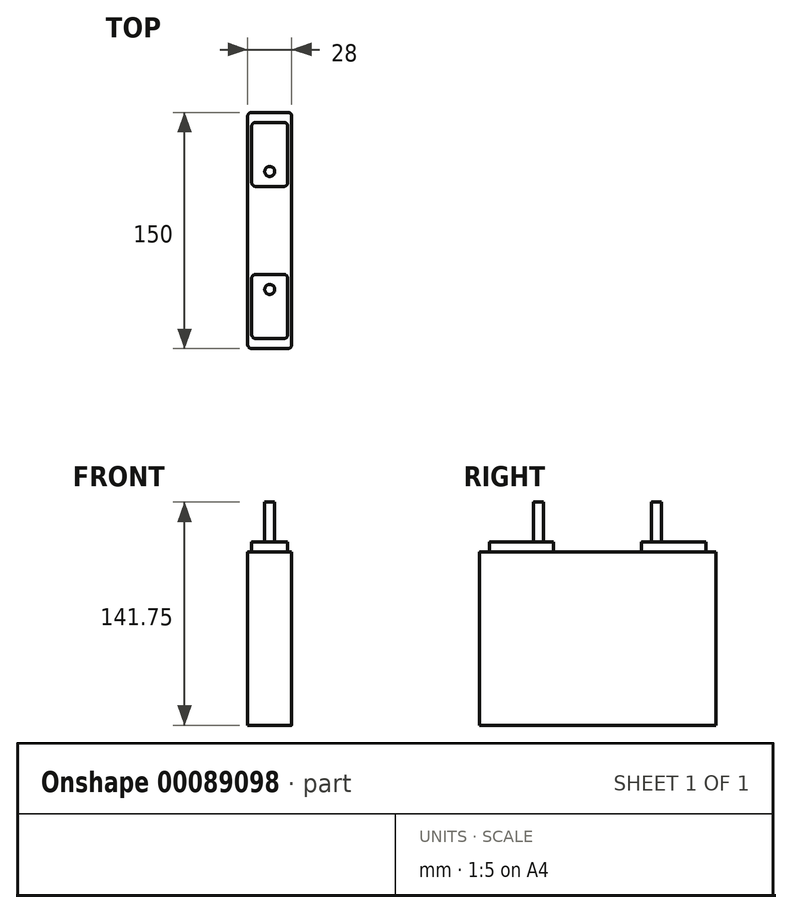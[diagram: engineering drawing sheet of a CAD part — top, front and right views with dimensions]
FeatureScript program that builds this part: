
annotation { "Feature Type Name" : "Feature", "Feature Type Description" : "" }
export const myFeature = defineFeature(function(context is Context, id is Id, definition is map)
    precondition{}
    {
        {
            var Q0;
            Q0=qCreatedBy(makeId("Top.planeOp"),FACE);
            var sketch = newSketch(context, id + "F0", { "sketchPlane" : qUnion([Q0])});
            skLineSegment(sketch, "E0.bottom", {"start": v(11.46, 75) * mm, "end": v(-11.46, 75) * mm});
            skLineSegment(sketch, "E0.top", {"start": v(11.46, -75) * mm, "end": v(-11.46, -75) * mm});
            skLineSegment(sketch, "E0.left", {"start": v(14, 72.46) * mm, "end": v(14, -72.46) * mm});
            skLineSegment(sketch, "E0.right", {"start": v(-14, 72.46) * mm, "end": v(-14, -72.46) * mm});
            skPoint(sketch, "E0.middle", {"position": v(0, 0) * mm});
            skPoint(sketch, "E1.visualSharp", {"position": v(14, -75) * mm});
            skArc(sketch, "E1.filletArc", {"start": v(11.46, -75) * mm, "mid": v(13.26, -74.26) * mm, "end": v(14, -72.46) * mm});
            skPoint(sketch, "E2.visualSharp", {"position": v(-14, -75) * mm});
            skArc(sketch, "E2.filletArc", {"start": v(-14, -72.46) * mm, "mid": v(-13.26, -74.26) * mm, "end": v(-11.46, -75) * mm});
            skPoint(sketch, "E3.visualSharp", {"position": v(-14, 75) * mm});
            skArc(sketch, "E3.filletArc", {"start": v(-11.46, 75) * mm, "mid": v(-13.26, 74.26) * mm, "end": v(-14, 72.46) * mm});
            skPoint(sketch, "E4.visualSharp", {"position": v(14, 75) * mm});
            skArc(sketch, "E4.filletArc", {"start": v(14, 72.46) * mm, "mid": v(13.26, 74.26) * mm, "end": v(11.46, 75) * mm});
            skSolve(sketch);
        }
        {
            var Q0;
            Q0 = qSketchRegion(id + "F0", true);
            extrude(context, id + "F1", {"entities" : qUnion([Q0]), "depth" : 110 * mm});
        }
        {
            var Q0;
            Q0=makeQuery(id+"F1.opExtrude","CAP_FACE",FACE,{"disambiguationData":[OSD([sQuery(id+"F0.wireOp",EDGE,"E0.bottom"),sQuery(id+"F0.wireOp",EDGE,"E0.top"),sQuery(id+"F0.wireOp",EDGE,"E0.left"),sQuery(id+"F0.wireOp",EDGE,"E0.right"),sQuery(id+"F0.wireOp",EDGE,"E1.filletArc"),sQuery(id+"F0.wireOp",EDGE,"E2.filletArc"),sQuery(id+"F0.wireOp",EDGE,"E3.filletArc"),sQuery(id+"F0.wireOp",EDGE,"E4.filletArc")])],"isStart":false});
            var sketch = newSketch(context, id + "F2", { "sketchPlane" : qUnion([Q0])});
            skLineSegment(sketch, "E5.bottom", {"start": v(-8.92, -68.65) * mm, "end": v(8.92, -68.65) * mm});
            skLineSegment(sketch, "E5.top", {"start": v(-8.92, -27.94) * mm, "end": v(8.92, -27.94) * mm});
            skLineSegment(sketch, "E5.left", {"start": v(-11.46, -66.11) * mm, "end": v(-11.46, -30.48) * mm});
            skLineSegment(sketch, "E5.right", {"start": v(11.46, -66.11) * mm, "end": v(11.46, -30.48) * mm});
            skLineSegment(sketch, "E6.bottom", {"start": v(-8.92, 68.65) * mm, "end": v(8.92, 68.65) * mm});
            skLineSegment(sketch, "E6.top", {"start": v(-8.92, 27.94) * mm, "end": v(8.92, 27.94) * mm});
            skLineSegment(sketch, "E6.left", {"start": v(-11.46, 66.11) * mm, "end": v(-11.46, 30.48) * mm});
            skLineSegment(sketch, "E6.right", {"start": v(11.46, 66.11) * mm, "end": v(11.46, 30.48) * mm});
            skPoint(sketch, "E7.visualSharp", {"position": v(11.46, -68.65) * mm});
            skArc(sketch, "E7.filletArc", {"start": v(8.92, -68.65) * mm, "mid": v(10.72, -67.9) * mm, "end": v(11.46, -66.11) * mm});
            skPoint(sketch, "E8.visualSharp", {"position": v(-11.46, -68.65) * mm});
            skArc(sketch, "E8.filletArc", {"start": v(-11.46, -66.11) * mm, "mid": v(-10.72, -67.9) * mm, "end": v(-8.92, -68.65) * mm});
            skPoint(sketch, "E9.visualSharp", {"position": v(-11.46, -27.94) * mm});
            skArc(sketch, "E9.filletArc", {"start": v(-8.92, -27.94) * mm, "mid": v(-10.72, -28.68) * mm, "end": v(-11.46, -30.48) * mm});
            skPoint(sketch, "E10.visualSharp", {"position": v(11.46, -27.94) * mm});
            skArc(sketch, "E10.filletArc", {"start": v(11.46, -30.48) * mm, "mid": v(10.72, -28.68) * mm, "end": v(8.92, -27.94) * mm});
            skPoint(sketch, "E11.visualSharp", {"position": v(11.46, 27.94) * mm});
            skArc(sketch, "E11.filletArc", {"start": v(8.92, 27.94) * mm, "mid": v(10.72, 28.68) * mm, "end": v(11.46, 30.48) * mm});
            skPoint(sketch, "E12.visualSharp", {"position": v(11.46, 68.65) * mm});
            skArc(sketch, "E12.filletArc", {"start": v(11.46, 66.11) * mm, "mid": v(10.72, 67.9) * mm, "end": v(8.92, 68.65) * mm});
            skPoint(sketch, "E13.visualSharp", {"position": v(-11.46, 68.65) * mm});
            skArc(sketch, "E13.filletArc", {"start": v(-8.92, 68.65) * mm, "mid": v(-10.72, 67.9) * mm, "end": v(-11.46, 66.11) * mm});
            skPoint(sketch, "E14.visualSharp", {"position": v(-11.46, 27.94) * mm});
            skArc(sketch, "E14.filletArc", {"start": v(-11.46, 30.48) * mm, "mid": v(-10.72, 28.68) * mm, "end": v(-8.92, 27.94) * mm});
            skSolve(sketch);
        }
        {
            var Q0;
            Q0 = qSketchRegion(id + "F2", true);
            extrude(context, id + "F3", {"entities" : qUnion([Q0]), "operationType" : NewBodyOperationType.ADD, "depth" : 6.35 * mm});
        }
        {
            var Q0;
            Q0=makeQuery(id+"F3.opExtrude","CAP_FACE",FACE,{"disambiguationData":[OSD([sQuery(id+"F2.wireOp",EDGE,"E5.bottom"),sQuery(id+"F2.wireOp",EDGE,"E5.top"),sQuery(id+"F2.wireOp",EDGE,"E5.left"),sQuery(id+"F2.wireOp",EDGE,"E5.right"),sQuery(id+"F2.wireOp",EDGE,"E7.filletArc"),sQuery(id+"F2.wireOp",EDGE,"E8.filletArc"),sQuery(id+"F2.wireOp",EDGE,"E9.filletArc"),sQuery(id+"F2.wireOp",EDGE,"E10.filletArc")])],"isStart":false});
            var sketch = newSketch(context, id + "F4", { "sketchPlane" : qUnion([Q0])});
            skCircle(sketch, "E15", {"center": v(0, -37.47) * mm, "radius": 3.18 * mm});
            skCircle(sketch, "E16", {"center": v(0, 37.47) * mm, "radius": 3.18 * mm});
            skLineSegment(sketch, "E17", {"start": v(0, -68.65) * mm, "end": v(0, 68.65) * mm, "construction": true});
            skSolve(sketch);
        }
        {
            var Q0;
            Q0 = qSketchRegion(id + "F4", true);
            extrude(context, id + "F5", {"entities" : qUnion([Q0]), "operationType" : NewBodyOperationType.ADD, "depth" : 25.4 * mm});
        }
    });
